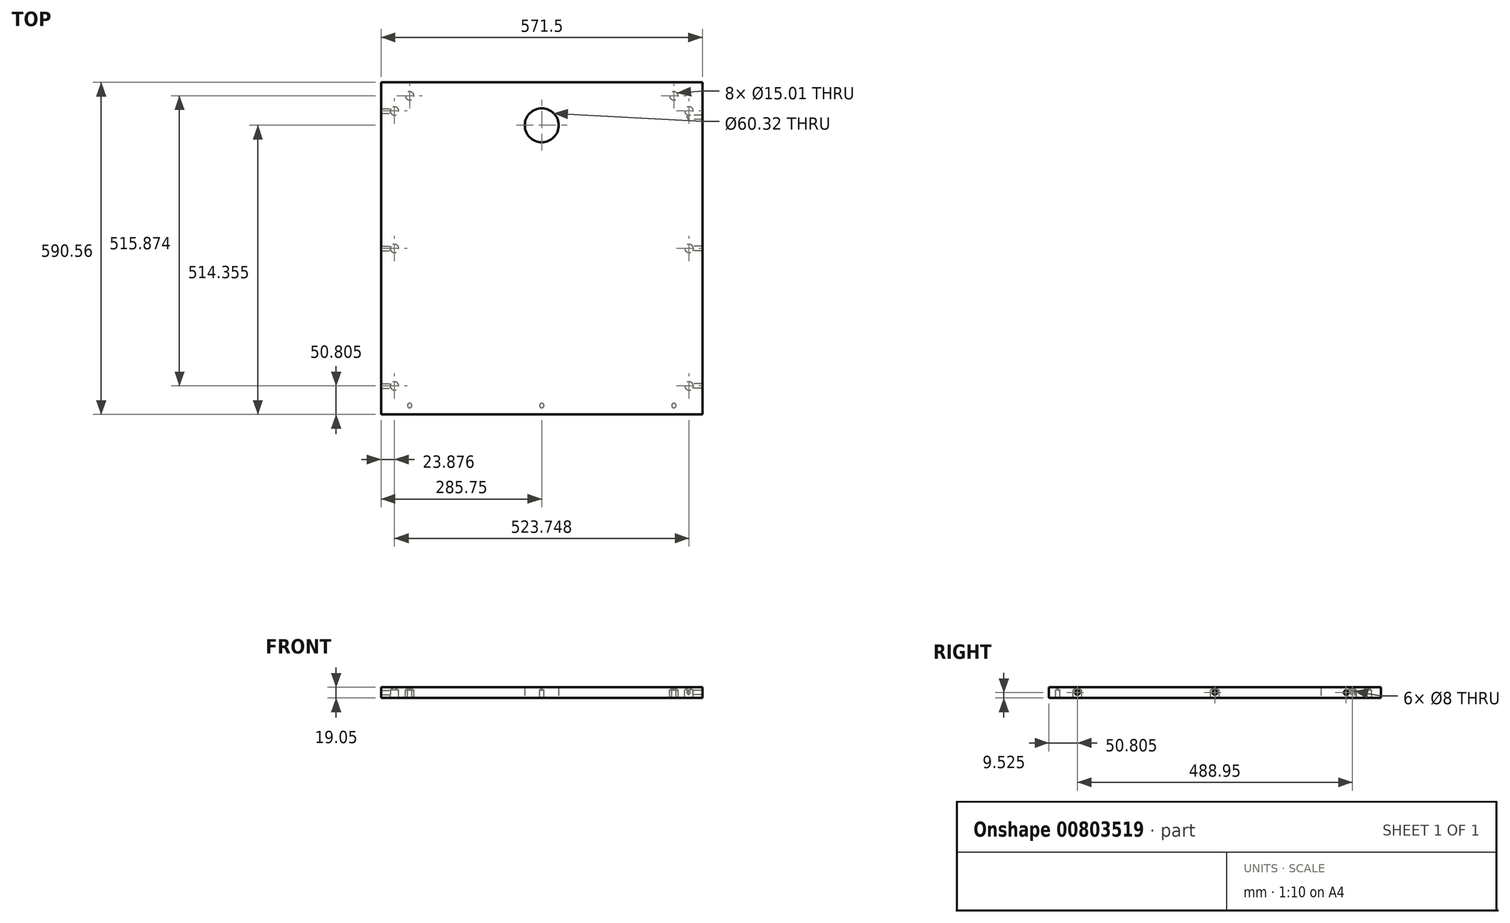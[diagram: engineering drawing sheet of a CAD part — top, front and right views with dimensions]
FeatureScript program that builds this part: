
annotation { "Feature Type Name" : "Feature", "Feature Type Description" : "" }
export const myFeature = defineFeature(function(context is Context, id is Id, definition is map)
    precondition{}
    {
        {
            var Q0;
            Q0=qCreatedBy(makeId("Top.planeOp"),FACE);
            var sketch = newSketch(context, id + "F0", { "sketchPlane" : qUnion([Q0])});
            skLineSegment(sketch, "E0.bottom", {"start": v(285.75, 295.28) * mm, "end": v(-285.75, 295.28) * mm});
            skLineSegment(sketch, "E0.top", {"start": v(285.75, -295.27) * mm, "end": v(-285.75, -295.28) * mm});
            skLineSegment(sketch, "E0.left", {"start": v(285.75, 295.28) * mm, "end": v(285.75, -295.27) * mm});
            skLineSegment(sketch, "E0.right", {"start": v(-285.75, 295.28) * mm, "end": v(-285.75, -295.28) * mm});
            skPoint(sketch, "E0.middle", {"position": v(0, 0) * mm});
            skLineSegment(sketch, "E1", {"start": v(0, 295.28) * mm, "end": v(0, 219.08) * mm});
            skCircle(sketch, "E2", {"center": v(0, 219.08) * mm, "radius": 30.16 * mm});
            skSolve(sketch);
        }
        {
            var Q0;
            Q0=makeQuery(id+"F0.imprint","IMPRINT",FACE,{"disambiguationData":[TD([[makeQuery(id+"F0.imprint","IMPRINT",EDGE,{"derivedFrom":sQuery(id+"F0.wireOp",EDGE,"E0.top")}),-1.0]])]});
            extrude(context, id + "F1", {"entities" : qUnion([Q0]), "depth" : 19.05 * mm, "offsetDistance" : 25.4 * mm});
        }
        {
            var Q0;
            Q0=makeQuery(id+"F1.opExtrude","CAP_FACE",FACE,{"disambiguationData":[OSD([sQuery(id+"F0.wireOp",EDGE,"E0.bottom"),sQuery(id+"F0.wireOp",EDGE,"E0.top"),sQuery(id+"F0.wireOp",EDGE,"E0.left"),sQuery(id+"F0.wireOp",EDGE,"E0.right"),sQuery(id+"F0.wireOp",EDGE,"E2")])],"isStart":true});
            var sketch = newSketch(context, id + "F2", { "sketchPlane" : qUnion([Q0])});
            skLineSegment(sketch, "E3", {"start": v(-285.75, 295.28) * mm, "end": v(-261.87, 295.28) * mm});
            skLineSegment(sketch, "E4", {"start": v(-261.87, 295.28) * mm, "end": v(-261.87, 244.48) * mm});
            skLineSegment(sketch, "E5", {"start": v(-285.75, -295.27) * mm, "end": v(-261.87, -295.27) * mm});
            skLineSegment(sketch, "E6", {"start": v(-261.87, -295.27) * mm, "end": v(-261.87, -244.47) * mm});
            skLineSegment(sketch, "E7", {"start": v(-285.75, 0) * mm, "end": v(-261.87, 0) * mm});
            skLineSegment(sketch, "E8", {"start": v(285.75, 0) * mm, "end": v(261.87, 0) * mm});
            skLineSegment(sketch, "E9", {"start": v(285.75, 295.28) * mm, "end": v(261.87, 295.28) * mm});
            skLineSegment(sketch, "E10", {"start": v(261.87, 295.28) * mm, "end": v(261.87, 244.48) * mm});
            skLineSegment(sketch, "E11", {"start": v(285.75, -295.27) * mm, "end": v(261.87, -295.27) * mm});
            skLineSegment(sketch, "E12", {"start": v(261.87, -295.27) * mm, "end": v(261.87, -244.47) * mm});
            skPoint(sketch, "E13", {"position": v(-261.87, 244.48) * mm});
            skPoint(sketch, "E14", {"position": v(-261.87, 0) * mm});
            skPoint(sketch, "E15", {"position": v(-261.87, -244.47) * mm});
            skPoint(sketch, "E16", {"position": v(261.87, -244.47) * mm});
            skPoint(sketch, "E17", {"position": v(261.87, 0) * mm});
            skPoint(sketch, "E18", {"position": v(261.87, 244.48) * mm});
            skSolve(sketch);
        }
        {
            var Q0;
            Q0=sQuery(id+"F2.wireOp",VERTEX,"E13");
            var Q1;
            Q1=sQuery(id+"F2.wireOp",VERTEX,"E18");
            var Q2;
            Q2=sQuery(id+"F2.wireOp",VERTEX,"E14");
            var Q3;
            Q3=sQuery(id+"F2.wireOp",VERTEX,"E17");
            var Q4;
            Q4=sQuery(id+"F2.wireOp",VERTEX,"E16");
            var Q5;
            Q5=sQuery(id+"F2.wireOp",VERTEX,"E15");
            var Q6;
            Q6=makeQuery(id+"F1.opExtrude","SWEPT_BODY",BODY,{"disambiguationData":[OSD([sQuery(id+"F0.wireOp",EDGE,"E0.bottom"),sQuery(id+"F0.wireOp",EDGE,"E0.top"),sQuery(id+"F0.wireOp",EDGE,"E0.left"),sQuery(id+"F0.wireOp",EDGE,"E0.right"),sQuery(id+"F0.wireOp",EDGE,"E2")])]});
            hole(context, id + "F3", {"style" : HoleStyle.SIMPLE, "endStyle" : HoleEndStyle.BLIND, "holeDiameter" : 15 * mm, "majorDiameter" : 6.35 * mm, "holeDepth" : 14.22 * mm, "isTappedThrough" : true, "tappedDepth" : 12.7 * mm, "tapClearance" : 3, "startFromSketch" : true, "locations" : qUnion([Q0, Q1, Q2, Q3, Q4, Q5]), "scope" : qUnion([Q6])});
        }
        {
            var Q0;
            Q0=makeQuery(id+"F1.opExtrude","SWEPT_FACE",FACE,{"disambiguationData":[OSD([sQuery(id+"F0.wireOp",EDGE,"E0.left")])]});
            var sketch = newSketch(context, id + "F4", { "sketchPlane" : qUnion([Q0])});
            skPoint(sketch, "E19", {"position": v(0, 9.52) * mm});
            skPoint(sketch, "E19.positionSnap0", {"position": v(0, 19.05) * mm});
            skPoint(sketch, "E20", {"position": v(-244.47, 9.52) * mm});
            skPoint(sketch, "E21", {"position": v(233.36, 9.52) * mm});
            skLineSegment(sketch, "E22", {"start": v(-244.47, 9.52) * mm, "end": v(-244.47, 0) * mm});
            skLineSegment(sketch, "E23", {"start": v(-244.47, 0) * mm, "end": v(-295.27, 0) * mm});
            skLineSegment(sketch, "E24", {"start": v(0, 0) * mm, "end": v(0, 9.53) * mm});
            skPoint(sketch, "E25", {"position": v(0, 9.53) * mm});
            skLineSegment(sketch, "E26", {"start": v(233.36, 9.52) * mm, "end": v(233.36, 0) * mm});
            skSolve(sketch);
        }
        {
            var Q0;
            Q0=sQuery(id+"F4.wireOp",VERTEX,"E20");
            var Q1;
            Q1=sQuery(id+"F4.wireOp",VERTEX,"E19");
            var Q2;
            Q2=sQuery(id+"F4.wireOp",VERTEX,"E21");
            var Q3;
            Q3=makeQuery(id+"F1.opExtrude","SWEPT_BODY",BODY,{"disambiguationData":[OSD([sQuery(id+"F0.wireOp",EDGE,"E0.bottom"),sQuery(id+"F0.wireOp",EDGE,"E0.top"),sQuery(id+"F0.wireOp",EDGE,"E0.left"),sQuery(id+"F0.wireOp",EDGE,"E0.right"),sQuery(id+"F0.wireOp",EDGE,"E2")])]});
            hole(context, id + "F5", {"style" : HoleStyle.SIMPLE, "endStyle" : HoleEndStyle.BLIND, "holeDiameter" : 8 * mm, "majorDiameter" : 6.35 * mm, "holeDepth" : 25.4 * mm, "isTappedThrough" : true, "tappedDepth" : 12.7 * mm, "tapClearance" : 3, "startFromSketch" : true, "locations" : qUnion([Q0, Q1, Q2]), "scope" : qUnion([Q3])});
        }
        {
            var Q0;
            Q0=makeQuery(id+"F1.opExtrude","SWEPT_FACE",FACE,{"disambiguationData":[OSD([sQuery(id+"F0.wireOp",EDGE,"E0.right")])]});
            var sketch = newSketch(context, id + "F6", { "sketchPlane" : qUnion([Q0])});
            skPoint(sketch, "E27", {"position": v(-244.47, 9.52) * mm});
            skPoint(sketch, "E28", {"position": v(244.47, 9.53) * mm});
            skLineSegment(sketch, "E29", {"start": v(0, 0) * mm, "end": v(0, 9.53) * mm});
            skPoint(sketch, "E30", {"position": v(0, 9.53) * mm});
            skLineSegment(sketch, "E31", {"start": v(-244.47, 9.52) * mm, "end": v(-244.47, 0) * mm});
            skLineSegment(sketch, "E32", {"start": v(-244.47, 0) * mm, "end": v(-295.28, 0) * mm});
            skLineSegment(sketch, "E33", {"start": v(244.47, 9.53) * mm, "end": v(244.47, 0) * mm});
            skLineSegment(sketch, "E34", {"start": v(244.47, 0) * mm, "end": v(295.28, 0) * mm});
            skSolve(sketch);
        }
        {
            var Q0;
            Q0=sQuery(id+"F6.wireOp",VERTEX,"7JFDCdo1-Y3dr-wsHc-LP2G-7qkS5dpKQL4z.end");
            var Q1;
            Q1=sQuery(id+"F6.wireOp",VERTEX,"E30");
            var Q2;
            Q2=sQuery(id+"F6.wireOp",VERTEX,"E28");
            var Q3;
            Q3=sQuery(id+"F6.wireOp",VERTEX,"E27");
            var Q4;
            Q4=makeQuery(id+"F1.opExtrude","SWEPT_BODY",BODY,{"disambiguationData":[OSD([sQuery(id+"F0.wireOp",EDGE,"E0.bottom"),sQuery(id+"F0.wireOp",EDGE,"E0.top"),sQuery(id+"F0.wireOp",EDGE,"E0.left"),sQuery(id+"F0.wireOp",EDGE,"E0.right"),sQuery(id+"F0.wireOp",EDGE,"E2")])]});
            hole(context, id + "F7", {"style" : HoleStyle.SIMPLE, "endStyle" : HoleEndStyle.BLIND, "holeDiameter" : 8 * mm, "majorDiameter" : 6.35 * mm, "holeDepth" : 25.4 * mm, "isTappedThrough" : true, "tappedDepth" : 12.7 * mm, "tapClearance" : 3, "startFromSketch" : true, "locations" : qUnion([Q0, Q1, Q2, Q3]), "scope" : qUnion([Q4])});
        }
        {
            var Q0;
            Q0=makeQuery(id+"F1.opExtrude","CAP_FACE",FACE,{"disambiguationData":[OSD([sQuery(id+"F0.wireOp",EDGE,"E0.bottom"),sQuery(id+"F0.wireOp",EDGE,"E0.top"),sQuery(id+"F0.wireOp",EDGE,"E0.left"),sQuery(id+"F0.wireOp",EDGE,"E0.right"),sQuery(id+"F0.wireOp",EDGE,"E2")])],"isStart":true});
            var sketch = newSketch(context, id + "F8", { "sketchPlane" : qUnion([Q0])});
            skLineSegment(sketch, "E35", {"start": v(-285.75, 295.28) * mm, "end": v(-285.75, 288.93) * mm});
            skLineSegment(sketch, "E36.bottom", {"start": v(-285.75, 288.93) * mm, "end": v(285.75, 288.93) * mm});
            skLineSegment(sketch, "E36.top", {"start": v(-285.75, 269.88) * mm, "end": v(285.75, 269.88) * mm});
            skLineSegment(sketch, "E36.left", {"start": v(-285.75, 288.93) * mm, "end": v(-285.75, 269.87) * mm});
            skLineSegment(sketch, "E36.right", {"start": v(285.75, 288.93) * mm, "end": v(285.75, 269.88) * mm});
            skLineSegment(sketch, "E37", {"start": v(-285.75, 279.4) * mm, "end": v(-234.95, 279.4) * mm});
            skLineSegment(sketch, "E38", {"start": v(285.75, 279.4) * mm, "end": v(234.95, 279.4) * mm});
            skLineSegment(sketch, "E39", {"start": v(0, 269.88) * mm, "end": v(0, 288.93) * mm});
            skPoint(sketch, "E40", {"position": v(-234.95, 279.4) * mm});
            skPoint(sketch, "E41", {"position": v(0, 279.4) * mm});
            skPoint(sketch, "E42", {"position": v(234.95, 279.4) * mm});
            skSolve(sketch);
        }
        {
            var Q0;
            Q0=sQuery(id+"F8.wireOp",VERTEX,"E40");
            var Q1;
            Q1=sQuery(id+"F8.wireOp",VERTEX,"E41");
            var Q2;
            Q2=sQuery(id+"F8.wireOp",VERTEX,"E42");
            var Q3;
            Q3=makeQuery(id+"F1.opExtrude","SWEPT_BODY",BODY,{"disambiguationData":[OSD([sQuery(id+"F0.wireOp",EDGE,"E0.bottom"),sQuery(id+"F0.wireOp",EDGE,"E0.top"),sQuery(id+"F0.wireOp",EDGE,"E0.left"),sQuery(id+"F0.wireOp",EDGE,"E0.right"),sQuery(id+"F0.wireOp",EDGE,"E2")])]});
            hole(context, id + "F9", {"style" : HoleStyle.SIMPLE, "endStyle" : HoleEndStyle.BLIND, "holeDiameter" : 8 * mm, "majorDiameter" : 6.35 * mm, "holeDepth" : 14.22 * mm, "isTappedThrough" : true, "tappedDepth" : 12.7 * mm, "tapClearance" : 3, "startFromSketch" : true, "locations" : qUnion([Q0, Q1, Q2]), "scope" : qUnion([Q3])});
        }
        {
            var Q0;
            Q0=makeQuery(id+"F1.opExtrude","CAP_FACE",FACE,{"disambiguationData":[OSD([sQuery(id+"F0.wireOp",EDGE,"E0.bottom"),sQuery(id+"F0.wireOp",EDGE,"E0.top"),sQuery(id+"F0.wireOp",EDGE,"E0.left"),sQuery(id+"F0.wireOp",EDGE,"E0.right"),sQuery(id+"F0.wireOp",EDGE,"E2")])],"isStart":true});
            var sketch = newSketch(context, id + "F10", { "sketchPlane" : qUnion([Q0])});
            skLineSegment(sketch, "E43", {"start": v(-285.75, -295.27) * mm, "end": v(-234.95, -295.27) * mm});
            skLineSegment(sketch, "E44", {"start": v(-234.95, -295.27) * mm, "end": v(-234.95, -271.4) * mm});
            skLineSegment(sketch, "E45", {"start": v(285.75, -295.28) * mm, "end": v(234.95, -295.28) * mm});
            skLineSegment(sketch, "E46", {"start": v(234.95, -295.28) * mm, "end": v(234.95, -271.4) * mm});
            skPoint(sketch, "E47", {"position": v(-234.95, -271.4) * mm});
            skPoint(sketch, "E48", {"position": v(234.95, -271.4) * mm});
            skSolve(sketch);
        }
        {
            var Q0;
            Q0=sQuery(id+"F10.wireOp",VERTEX,"E47");
            var Q1;
            Q1=sQuery(id+"F10.wireOp",VERTEX,"E48");
            var Q2;
            Q2=makeQuery(id+"F1.opExtrude","SWEPT_BODY",BODY,{"disambiguationData":[OSD([sQuery(id+"F0.wireOp",EDGE,"E0.bottom"),sQuery(id+"F0.wireOp",EDGE,"E0.top"),sQuery(id+"F0.wireOp",EDGE,"E0.left"),sQuery(id+"F0.wireOp",EDGE,"E0.right"),sQuery(id+"F0.wireOp",EDGE,"E2")])]});
            hole(context, id + "F11", {"style" : HoleStyle.SIMPLE, "endStyle" : HoleEndStyle.BLIND, "holeDiameter" : 15 * mm, "majorDiameter" : 6.35 * mm, "holeDepth" : 14.22 * mm, "isTappedThrough" : true, "tappedDepth" : 12.7 * mm, "tapClearance" : 3, "startFromSketch" : true, "locations" : qUnion([Q0, Q1]), "scope" : qUnion([Q2])});
        }
    });
